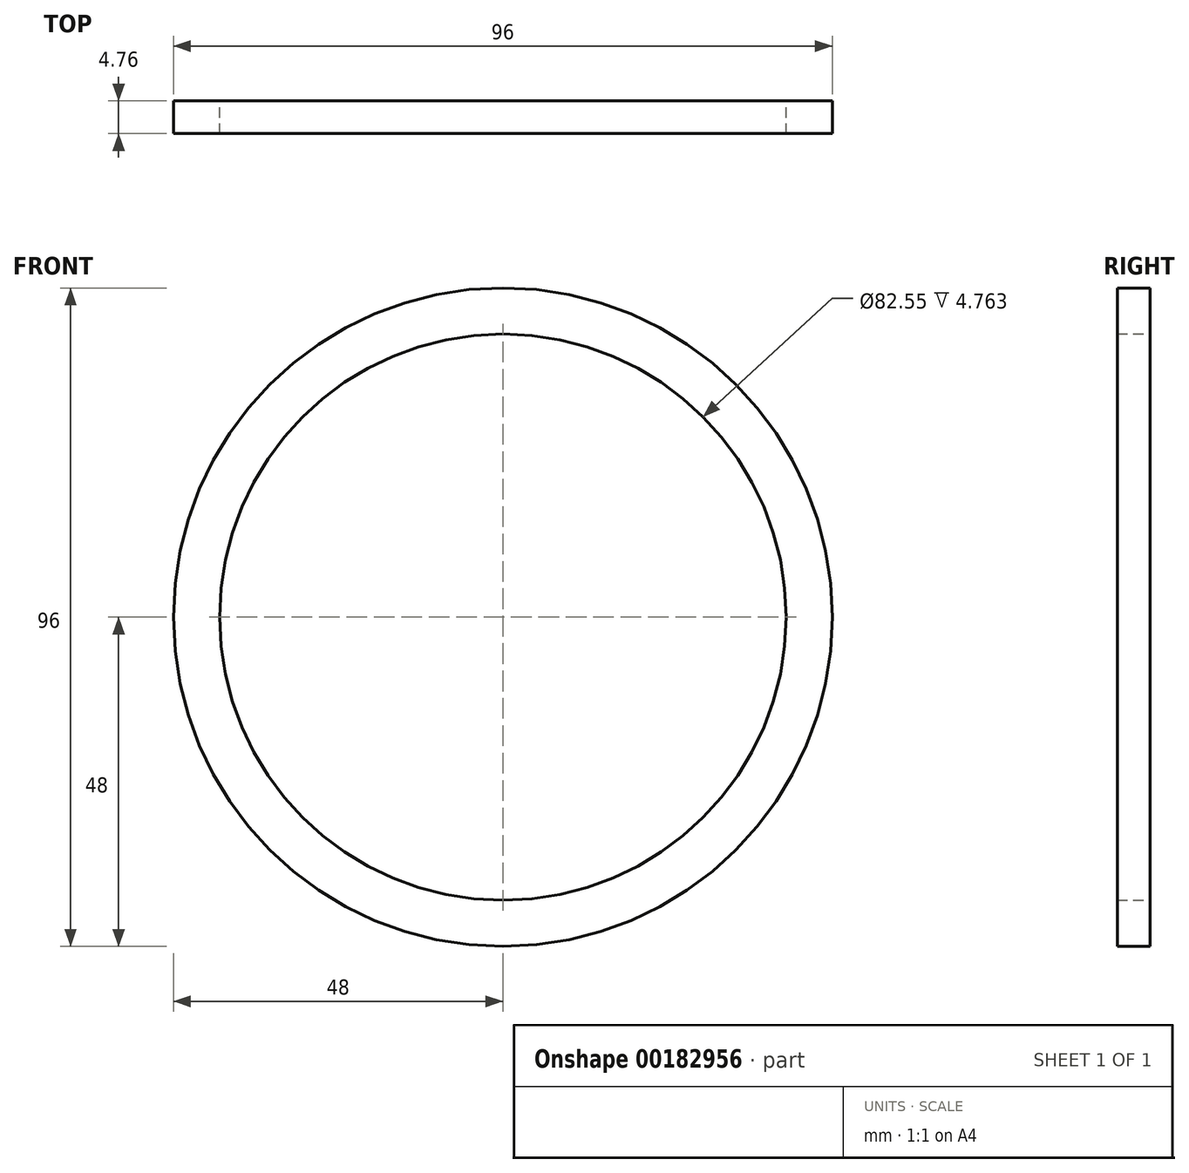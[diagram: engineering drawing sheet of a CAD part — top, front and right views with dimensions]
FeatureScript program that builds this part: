
annotation { "Feature Type Name" : "Feature", "Feature Type Description" : "" }
export const myFeature = defineFeature(function(context is Context, id is Id, definition is map)
    precondition{}
    {
        {
            var Q0;
            Q0=qCreatedBy(makeId("Front.planeOp"),FACE);
            var sketch = newSketch(context, id + "F0", { "sketchPlane" : qUnion([Q0])});
            skCircle(sketch, "E0", {"center": v(0, 0) * mm, "radius": 48 * mm});
            skCircle(sketch, "E1", {"center": v(0, 0) * mm, "radius": 1.5 * mm});
            skCircle(sketch, "E2", {"center": v(0, 0) * mm, "radius": 41.28 * mm});
            skSolve(sketch);
        }
        {
            var Q0;
            Q0=makeQuery(id+"F0.imprint","IMPRINT",FACE,{"disambiguationData":[TD([[makeQuery(id+"F0.imprint","IMPRINT",EDGE,{"derivedFrom":sQuery(id+"F0.wireOp",EDGE,"E0")}),1.0]])]});
            var Q1;
            Q1=sQuery(id+"F0.wireOp",EDGE,"E1");
            var Q2;
            Q2=sQuery(id+"F0.wireOp",EDGE,"E0");
            extrude(context, id + "F1", {"entities" : qUnion([Q0]), "surfaceEntities" : qUnion([Q1, Q2]), "depth" : 4.76 * mm});
        }
    });
